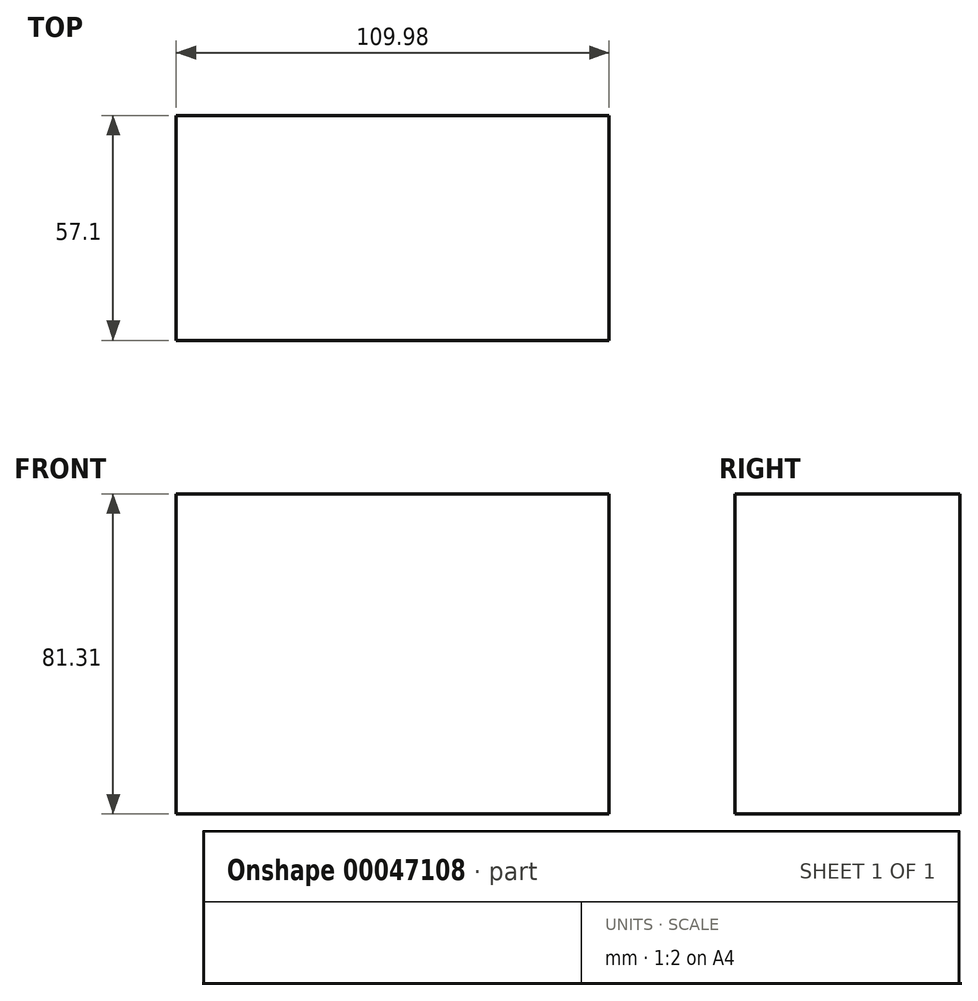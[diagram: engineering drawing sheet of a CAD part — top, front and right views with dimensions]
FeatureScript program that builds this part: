
annotation { "Feature Type Name" : "Feature", "Feature Type Description" : "" }
export const myFeature = defineFeature(function(context is Context, id is Id, definition is map)
    precondition{}
    {
        {
            var Q0;
            Q0=qCreatedBy(makeId("Right.planeOp"),FACE);
            cPlane(context, id + "F0", {"entities" : qUnion([Q0]), "cplaneType" : CPlaneType.OFFSET, "offset" : 20.32 * mm, "width" : 152.4 * mm, "height" : 152.4 * mm});
        }
        {
            var Q0;
            Q0=qCreatedBy(makeId("Right.planeOp"),FACE);
            var sketch = newSketch(context, id + "F1", { "sketchPlane" : qUnion([Q0])});
            skCircle(sketch, "E0", {"center": v(-11.6, 29.4) * mm, "radius": 31.6 * mm});
            skPoint(sketch, "E0.first.point", {"position": v(0, 0) * mm});
            skPoint(sketch, "E0.second.point", {"position": v(-16.36, 60.64) * mm});
            skPoint(sketch, "E0.third.point", {"position": v(-24.12, 0.38) * mm});
            skSolve(sketch);
        }
        {
            var Q0;
            Q0=makeQuery(id+"F1.imprint","IMPRINT",FACE,{"disambiguationData":[TD([[makeQuery(id+"F1.imprint","IMPRINT",EDGE,{"derivedFrom":sQuery(id+"F1.wireOp",EDGE,"E0")}),1.0]])]});
            var Q1;
            Q1=sQuery(id+"F1.wireOp",EDGE,"E0");
            extrude(context, id + "F2", {"entities" : qUnion([Q0]), "bodyType" : ToolBodyType.SURFACE, "surfaceEntities" : qUnion([Q1]), "oppositeDirection" : true, "depth" : 64.48 * mm});
        }
        {
            var Q0;
            Q0=qCreatedBy(id+"F0.planeOp",FACE);
            var sketch = newSketch(context, id + "F3", { "sketchPlane" : qUnion([Q0])});
            skCircle(sketch, "E1", {"center": v(-11.6, 29.4) * mm, "radius": 23.22 * mm});
            skFitSpline(sketch, "E2", {"points": [v(-55.18, 70.48) * mm, v(-36.3, 54.88) * mm, v(30.1, 69.73) * mm, v(49.41, 21.32) * mm, v(-33.6, -25.33) * mm, v(-61.2, 54.68) * mm, v(-55.18, 70.48) * mm]});
            skSolve(sketch);
        }
        {
            var Q0;
            Q0=makeQuery(id+"F3.imprint","IMPRINT",FACE,{"disambiguationData":[TD([[makeQuery(id+"F3.imprint","IMPRINT",EDGE,{"derivedFrom":sQuery(id+"F3.wireOp",EDGE,"E1")}),-1.0]])]});
            var Q1;
            Q1=sQuery(id+"F3.wireOp",EDGE,"E2");
            var Q2;
            Q2=makeQuery(id+"F2.opExtrude","CAP_EDGE",EDGE,{"disambiguationData":[OSD([sQuery(id+"F1.wireOp",EDGE,"E0")])],"isStart":true});
            loft(context, id + "F4", {"bodyType" : ToolBodyType.SURFACE, "startCondition" : LoftEndDerivativeType.NORMAL_TO_PROFILE, "startMagnitude" : 1, "endCondition" : LoftEndDerivativeType.MATCH_CURVATURE, "endMagnitude" : 1, "sheetProfilesArray" : [{ "sheetProfileEntities" : qUnion([Q0]) }], "wireProfilesArray" : [{ "wireProfileEntities" : qUnion([Q1]) }, { "wireProfileEntities" : qUnion([Q2]) }]});
        }
        {
            var Q0;
            Q0=qCreatedBy(makeId("Right.planeOp"),FACE);
            var sketch = newSketch(context, id + "F5", { "sketchPlane" : qUnion([Q0])});
            skLineSegment(sketch, "E3.bottom", {"start": v(180.16, 25.69) * mm, "end": v(123.06, 25.69) * mm});
            skLineSegment(sketch, "E3.top", {"start": v(180.16, 107) * mm, "end": v(123.06, 107) * mm});
            skLineSegment(sketch, "E3.left", {"start": v(180.16, 25.69) * mm, "end": v(180.16, 107) * mm});
            skLineSegment(sketch, "E3.right", {"start": v(123.06, 25.69) * mm, "end": v(123.06, 107) * mm});
            skSolve(sketch);
        }
        {
            var Q0;
            Q0=makeQuery(id+"F5.imprint","IMPRINT",FACE,{"disambiguationData":[TD([[makeQuery(id+"F5.imprint","IMPRINT",EDGE,{"derivedFrom":sQuery(id+"F5.wireOp",EDGE,"E3.bottom")}),-1.0]])]});
            extrude(context, id + "F6", {"entities" : qUnion([Q0]), "oppositeDirection" : true, "depth" : 109.98 * mm, "offsetDistance" : 25.4 * mm});
        }
    });
